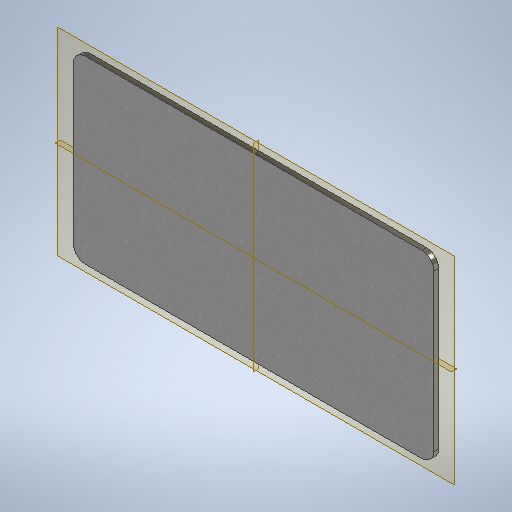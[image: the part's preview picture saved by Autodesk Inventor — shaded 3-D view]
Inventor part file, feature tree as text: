
AUTODESK INVENTOR PART (.ipt)
format: ipt  version: 2025.2 (Build 292293000, 293)  size: 292,864 bytes
history: native  units: mm
features: fillet x3, other x2, sheet_metal_op x1, sketch x1
ambient origin geometry x8: Origin, YZ Plane, XZ Plane, XY Plane, X Axis, Y Axis, Z Axis, Center Point
bodies: Body1 (feature_tree)
feature tree (7):
  other  "Sólido1"
  sheet_metal_op  "Face1"
  fillet  "Arredondamento1"  Radius=1500.0mm
  fillet  "Arredondamento2"  Radius=750.0mm
  fillet  "Arredondamento3"  Radius=20.0mm
  sketch  "Esboço1"  dims[d3=50.0mm d4=50.0mm d5=50.0mm]
  other  "Placa1"
